# Revit family: 120909-00126 Шкаф ШРП-В2400-Р-ПВТ-10 ССД
name_source: partatom
category: Обобщенные модели
units: mm (PartAtom-declared; Revit-internal decimal feet)

## family parameters
Всегда вертикально = Да
Может служить основой для арматурных стержней = Нет
На основе рабочей плоскости = Нет
Общий = Нет
При загрузке вырезать с полостями = Нет
Размер круглого соединителя = Использовать диаметр
Тип детали = Нормальный
Точка расчета площади = Нет

## types (1)
- ШРП-В/2400-Р-ПВТ-10 (240 плинтов ПВТ)
    ADSK_URL документации изделия = shr_decl_2017.pdf (ssd.ru)
    ADSK_URL страницы изделия = Шкаф ШРП-В/2400-Р-ПВТ-10 ССД ( 120909-00126 ) (ssd.ru)
    ADSK_Единица измерения = шт
    ADSK_Завод-изготовитель = АО СВЯЗЬСТРОЙДЕТАЛЬ
    ADSK_Код изделия = 120909-00126
    ADSK_Масса_Текст = 114
    ADSK_Наименование = Шкаф ШРП-В/2400-Р-ПВТ-10 ССД
    ADSK_Наименование краткое = ШРП-В/2400-Р-ПВТ-10 (240 плинтов ПВТ)
    ADSK_Размер_Высота = 2240 мм
    ADSK_Размер_Глубина = 300 мм
    ADSK_Размер_Ширина = 860 мм
    Материал Каркаса = RAL 7035
    Материал букв = Металл красный
    Ноль = 0 мм
    Описание = Шкаф ШРП-В/2400-Р-ПВТ-10 ССД
    Толщина -4 = -4 мм
    Толщина 25 = 25 мм
    Толщина 4 = 4 мм
    Толщина 5 = 5 мм

## geometry (parser evidence)
native form markers: Blend x2
no freeform markers — native parametric forms only
